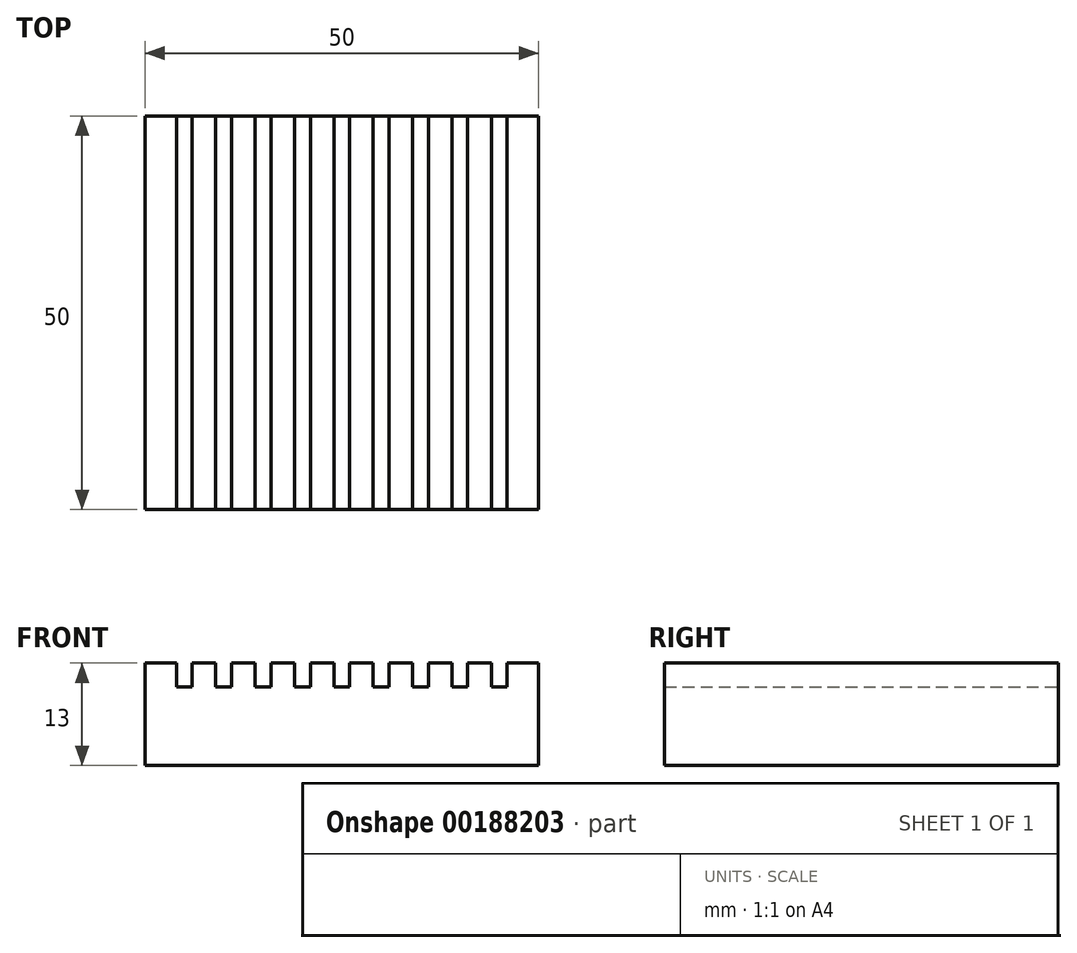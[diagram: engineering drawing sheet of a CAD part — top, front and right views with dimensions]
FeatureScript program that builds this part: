
annotation { "Feature Type Name" : "Feature", "Feature Type Description" : "" }
export const myFeature = defineFeature(function(context is Context, id is Id, definition is map)
    precondition{}
    {
        {
            var Q0;
            Q0=qCreatedBy(makeId("Top.planeOp"),FACE);
            var sketch = newSketch(context, id + "F0", { "sketchPlane" : qUnion([Q0])});
            skLineSegment(sketch, "E0.bottom", {"start": v(25, -25) * mm, "end": v(-25, -25) * mm});
            skLineSegment(sketch, "E0.top", {"start": v(25, 25) * mm, "end": v(-25, 25) * mm});
            skLineSegment(sketch, "E0.left", {"start": v(25, -25) * mm, "end": v(25, 25) * mm});
            skLineSegment(sketch, "E0.right", {"start": v(-25, -25) * mm, "end": v(-25, 25) * mm});
            skPoint(sketch, "E0.middle", {"position": v(0, 0) * mm});
            skSolve(sketch);
        }
        {
            var Q0;
            Q0 = qSketchRegion(id + "F0", true);
            extrude(context, id + "F1", {"entities" : qUnion([Q0]), "depth" : 13 * mm});
        }
        {
            var Q0;
            Q0=makeQuery(id+"F1.opExtrude","SWEPT_FACE",FACE,{"disambiguationData":[OSD([sQuery(id+"F0.wireOp",EDGE,"E0.top")])]});
            var sketch = newSketch(context, id + "F2", { "sketchPlane" : qUnion([Q0])});
            skLineSegment(sketch, "E1", {"start": v(-21, 13) * mm, "end": v(-21, 10) * mm});
            skLineSegment(sketch, "E2", {"start": v(-21, 10) * mm, "end": v(-19, 10) * mm});
            skLineSegment(sketch, "E3", {"start": v(-19, 10) * mm, "end": v(-19, 13) * mm});
            skLineSegment(sketch, "E4", {"start": v(-19, 13) * mm, "end": v(-16, 13) * mm});
            skLineSegment(sketch, "E5", {"start": v(-16, 13) * mm, "end": v(-16, 10) * mm});
            skLineSegment(sketch, "E6", {"start": v(-16, 10) * mm, "end": v(-14, 10) * mm});
            skLineSegment(sketch, "E7", {"start": v(-14, 10) * mm, "end": v(-14, 13) * mm});
            skLineSegment(sketch, "E8", {"start": v(-14, 13) * mm, "end": v(-11, 13) * mm});
            skLineSegment(sketch, "E9", {"start": v(-11, 13) * mm, "end": v(-11, 10) * mm});
            skLineSegment(sketch, "E10", {"start": v(-11, 10) * mm, "end": v(-9, 10) * mm});
            skLineSegment(sketch, "E11", {"start": v(-9, 10) * mm, "end": v(-9, 13) * mm});
            skLineSegment(sketch, "E12", {"start": v(-9, 13) * mm, "end": v(-6, 13) * mm});
            skLineSegment(sketch, "E13", {"start": v(-6, 13) * mm, "end": v(-6, 10) * mm});
            skLineSegment(sketch, "E14", {"start": v(-6, 10) * mm, "end": v(-4, 10) * mm});
            skLineSegment(sketch, "E15", {"start": v(-4, 10) * mm, "end": v(-4, 13) * mm});
            skLineSegment(sketch, "E16", {"start": v(-4, 13) * mm, "end": v(-1, 13) * mm});
            skLineSegment(sketch, "E17", {"start": v(-1, 13) * mm, "end": v(-1, 10) * mm});
            skLineSegment(sketch, "E18", {"start": v(-1, 10) * mm, "end": v(0, 10) * mm});
            skLineSegment(sketch, "E19.MirrorCS", {"start": v(1, 10) * mm, "end": v(0, 10) * mm});
            skLineSegment(sketch, "E20.MirrorCS", {"start": v(1, 13) * mm, "end": v(1, 10) * mm});
            skLineSegment(sketch, "E21.MirrorCS", {"start": v(4, 13) * mm, "end": v(1, 13) * mm});
            skLineSegment(sketch, "E22.MirrorCS", {"start": v(4, 10) * mm, "end": v(4, 13) * mm});
            skLineSegment(sketch, "E23.MirrorCS", {"start": v(6, 10) * mm, "end": v(4, 10) * mm});
            skLineSegment(sketch, "E24.MirrorCS", {"start": v(6, 13) * mm, "end": v(6, 10) * mm});
            skLineSegment(sketch, "E25.MirrorCS", {"start": v(9, 13) * mm, "end": v(6, 13) * mm});
            skLineSegment(sketch, "E26.MirrorCS", {"start": v(9, 10) * mm, "end": v(9, 13) * mm});
            skLineSegment(sketch, "E27.MirrorCS", {"start": v(11, 10) * mm, "end": v(9, 10) * mm});
            skLineSegment(sketch, "E28.MirrorCS", {"start": v(11, 13) * mm, "end": v(11, 10) * mm});
            skLineSegment(sketch, "E29.MirrorCS", {"start": v(14, 13) * mm, "end": v(11, 13) * mm});
            skLineSegment(sketch, "E30.MirrorCS", {"start": v(14, 10) * mm, "end": v(14, 13) * mm});
            skLineSegment(sketch, "E31.MirrorCS", {"start": v(16, 10) * mm, "end": v(14, 10) * mm});
            skLineSegment(sketch, "E32.MirrorCS", {"start": v(16, 13) * mm, "end": v(16, 10) * mm});
            skLineSegment(sketch, "E33.MirrorCS", {"start": v(19, 13) * mm, "end": v(16, 13) * mm});
            skLineSegment(sketch, "E34.MirrorCS", {"start": v(19, 10) * mm, "end": v(19, 13) * mm});
            skLineSegment(sketch, "E35.MirrorCS", {"start": v(21, 10) * mm, "end": v(19, 10) * mm});
            skLineSegment(sketch, "E36.MirrorCS", {"start": v(21, 13) * mm, "end": v(21, 10) * mm});
            skSolve(sketch);
        }
        {
            var Q0;
            {var subQ0=sQuery(id+"F2.wireOp",EDGE,"E1");Q0=makeQuery(id+"F2.imprint","IMPRINT",FACE,{"disambiguationData":[TD([[makeQuery(id+"F2.imprint","IMPRINT",EDGE,{"derivedFrom":subQ0}),1.0]])]});}
            var Q1;
            {var subQ0=sQuery(id+"F2.wireOp",EDGE,"E5");Q1=makeQuery(id+"F2.imprint","IMPRINT",FACE,{"disambiguationData":[TD([[makeQuery(id+"F2.imprint","IMPRINT",EDGE,{"derivedFrom":subQ0}),1.0]])]});}
            var Q2;
            {var subQ0=sQuery(id+"F2.wireOp",EDGE,"E9");Q2=makeQuery(id+"F2.imprint","IMPRINT",FACE,{"disambiguationData":[TD([[makeQuery(id+"F2.imprint","IMPRINT",EDGE,{"derivedFrom":subQ0}),1.0]])]});}
            var Q3;
            {var subQ0=sQuery(id+"F2.wireOp",EDGE,"E13");Q3=makeQuery(id+"F2.imprint","IMPRINT",FACE,{"disambiguationData":[TD([[makeQuery(id+"F2.imprint","IMPRINT",EDGE,{"derivedFrom":subQ0}),1.0]])]});}
            var Q4;
            {var subQ1=sQuery(id+"F2.wireOp",EDGE,"E17");Q4=makeQuery(id+"F2.imprint","IMPRINT",FACE,{"disambiguationData":[TD([[makeQuery(id+"F2.imprint","IMPRINT",EDGE,{"derivedFrom":subQ1}),1.0]])]});}
            var Q5;
            {var subQ0=sQuery(id+"F2.wireOp",EDGE,"E22.MirrorCS");Q5=makeQuery(id+"F2.imprint","IMPRINT",FACE,{"disambiguationData":[TD([[makeQuery(id+"F2.imprint","IMPRINT",EDGE,{"derivedFrom":subQ0}),-1.0]])]});}
            var Q6;
            {var subQ0=sQuery(id+"F2.wireOp",EDGE,"E26.MirrorCS");Q6=makeQuery(id+"F2.imprint","IMPRINT",FACE,{"disambiguationData":[TD([[makeQuery(id+"F2.imprint","IMPRINT",EDGE,{"derivedFrom":subQ0}),-1.0]])]});}
            var Q7;
            {var subQ0=sQuery(id+"F2.wireOp",EDGE,"E30.MirrorCS");Q7=makeQuery(id+"F2.imprint","IMPRINT",FACE,{"disambiguationData":[TD([[makeQuery(id+"F2.imprint","IMPRINT",EDGE,{"derivedFrom":subQ0}),-1.0]])]});}
            var Q8;
            {var subQ0=sQuery(id+"F2.wireOp",EDGE,"E34.MirrorCS");Q8=makeQuery(id+"F2.imprint","IMPRINT",FACE,{"disambiguationData":[TD([[makeQuery(id+"F2.imprint","IMPRINT",EDGE,{"derivedFrom":subQ0}),-1.0]])]});}
            extrude(context, id + "F3", {"entities" : qUnion([Q0, Q1, Q2, Q3, Q4, Q5, Q6, Q7, Q8]), "operationType" : NewBodyOperationType.REMOVE, "endBound" : BoundingType.THROUGH_ALL, "oppositeDirection" : true, "depth" : 25 * mm});
        }
    });
